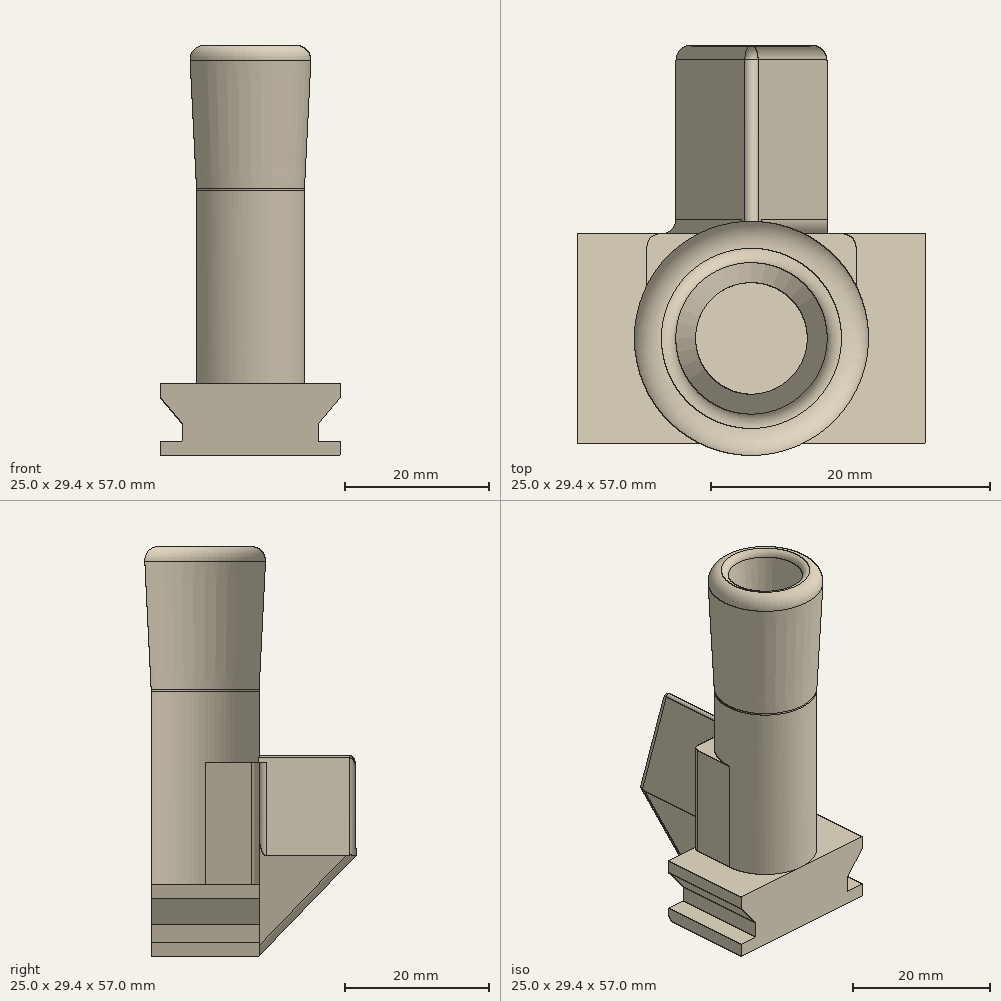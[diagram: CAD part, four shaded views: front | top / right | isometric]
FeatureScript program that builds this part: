
annotation { "Feature Type Name" : "Feature", "Feature Type Description" : "" }
export const myFeature = defineFeature(function(context is Context, id is Id, definition is map)
    precondition{}
    {
        {
            var Q0;
            Q0=qCreatedBy(makeId("Front.planeOp"),FACE);
            var sketch = newSketch(context, id + "F0", { "sketchPlane" : qUnion([Q0])});
            skLineSegment(sketch, "E0", {"start": v(0, 0) * mm, "end": v(0, 17.87) * mm, "construction": true});
            skLineSegment(sketch, "E1", {"start": v(0, 0) * mm, "end": v(-12.5, 0) * mm});
            skLineSegment(sketch, "E2", {"start": v(-12.5, 0) * mm, "end": v(-12.5, 2) * mm});
            skLineSegment(sketch, "E3", {"start": v(-12.5, 2) * mm, "end": v(-9.5, 2) * mm});
            skLineSegment(sketch, "E4", {"start": v(-9.5, 2) * mm, "end": v(-9.5, 4.42) * mm});
            skLineSegment(sketch, "E5", {"start": v(-12.5, 8) * mm, "end": v(-12.5, 10) * mm});
            skLineSegment(sketch, "E6", {"start": v(-12.5, 10) * mm, "end": v(0, 10) * mm});
            skLineSegment(sketch, "E7.MirrorCS", {"start": v(0, 0) * mm, "end": v(12.5, 0) * mm});
            skLineSegment(sketch, "E8.MirrorCS", {"start": v(12.5, 10) * mm, "end": v(0, 10) * mm});
            skLineSegment(sketch, "E9.MirrorCS", {"start": v(12.5, 8) * mm, "end": v(12.5, 10) * mm});
            skLineSegment(sketch, "E10.MirrorCS", {"start": v(12.5, 0) * mm, "end": v(12.5, 2) * mm});
            skLineSegment(sketch, "E11.MirrorCS", {"start": v(12.5, 2) * mm, "end": v(9.5, 2) * mm});
            skLineSegment(sketch, "E12", {"start": v(-12.5, 8) * mm, "end": v(-9.5, 4.42) * mm});
            skPoint(sketch, "E13.orphan", {"position": v(-9.5, 5.59) * mm});
            skLineSegment(sketch, "E14.MirrorCS", {"start": v(12.5, 8) * mm, "end": v(9.5, 4.42) * mm});
            skLineSegment(sketch, "E15.MirrorCS", {"start": v(9.5, 2) * mm, "end": v(9.5, 4.42) * mm});
            skSolve(sketch);
        }
        {
            var Q0;
            Q0 = qSketchRegion(id + "F0", true);
            extrude(context, id + "F1", {"entities" : qUnion([Q0]), "depth" : 15 * mm});
        }
        {
            var Q0;
            Q0=makeQuery(id+"F1.opExtrude","SWEPT_FACE",FACE,{"disambiguationData":[OSD([sQuery(id+"F0.wireOp",EDGE,"E6"),sQuery(id+"F0.wireOp",EDGE,"E8.MirrorCS")])]});
            var sketch = newSketch(context, id + "F2", { "sketchPlane" : qUnion([Q0])});
            skLineSegment(sketch, "E16", {"start": v(0, 0) * mm, "end": v(0, -15) * mm, "construction": true});
            skLineSegment(sketch, "E17", {"start": v(-7.5, -7.5) * mm, "end": v(-7.5, 0) * mm});
            skLineSegment(sketch, "E18", {"start": v(-7.5, 0) * mm, "end": v(7.5, 0) * mm});
            skLineSegment(sketch, "E19", {"start": v(7.5, 0) * mm, "end": v(7.5, -7.5) * mm});
            skLineSegment(sketch, "E20", {"start": v(-7.5, -7.5) * mm, "end": v(0, -7.5) * mm, "construction": true});
            skLineSegment(sketch, "E21", {"start": v(0, -7.5) * mm, "end": v(7.5, -7.5) * mm, "construction": true});
            skArc(sketch, "E22", {"start": v(-7.5, -7.5) * mm, "mid": v(0, -15) * mm, "end": v(7.5, -7.5) * mm});
            skSolve(sketch);
        }
        {
            var Q0;
            Q0 = qSketchRegion(id + "F2", true);
            extrude(context, id + "F3", {"entities" : qUnion([Q0]), "operationType" : NewBodyOperationType.ADD, "depth" : 5 * mm});
        }
        {
            var Q0;
            Q0=makeQuery(id+"F3.opExtrude","CAP_FACE",FACE,{"disambiguationData":[OSD([sQuery(id+"F2.wireOp",EDGE,"E17"),sQuery(id+"F2.wireOp",EDGE,"E18"),sQuery(id+"F2.wireOp",EDGE,"E19"),sQuery(id+"F2.wireOp",EDGE,"E22")])],"isStart":false});
            var sketch = newSketch(context, id + "F4", { "sketchPlane" : qUnion([Q0])});
            skArc(sketch, "E23.0", {"start": v(-7.5, -7.5) * mm, "mid": v(0, -15) * mm, "end": v(7.5, -7.5) * mm});
            skCircle(sketch, "E24", {"center": v(0, -7.5) * mm, "radius": 4 * mm});
            skLineSegment(sketch, "E25", {"start": v(-7.5, -7.5) * mm, "end": v(-7.5, 0) * mm});
            skLineSegment(sketch, "E26", {"start": v(-7.5, 0) * mm, "end": v(7.5, 0) * mm});
            skLineSegment(sketch, "E27", {"start": v(7.5, 0) * mm, "end": v(7.5, -7.5) * mm});
            skSolve(sketch);
        }
        {
            var Q0;
            Q0 = qSketchRegion(id + "F4", true);
            extrude(context, id + "F5", {"entities" : qUnion([Q0]), "operationType" : NewBodyOperationType.ADD, "depth" : 12 * mm});
        }
        {
            var Q0;
            Q0=makeQuery(id+"F5.opExtrude","CAP_FACE",FACE,{"disambiguationData":[OSD([sQuery(id+"F4.wireOp",EDGE,"E23.0"),sQuery(id+"F4.wireOp",EDGE,"E24"),sQuery(id+"F4.wireOp",EDGE,"E25"),sQuery(id+"F4.wireOp",EDGE,"E26"),sQuery(id+"F4.wireOp",EDGE,"E27")])],"isStart":false});
            var sketch = newSketch(context, id + "F6", { "sketchPlane" : qUnion([Q0])});
            skCircle(sketch, "E28.0", {"center": v(0, -7.5) * mm, "radius": 4 * mm});
            skCircle(sketch, "E29", {"center": v(0, -7.5) * mm, "radius": 7.5 * mm});
            skSolve(sketch);
        }
        {
            var Q0;
            Q0 = qSketchRegion(id + "F6", true);
            extrude(context, id + "F7", {"entities" : qUnion([Q0]), "operationType" : NewBodyOperationType.ADD, "depth" : 10 * mm});
        }
        {
            var Q0;
            Q0=makeQuery(id+"F5.boolean.opBoolean","MERGE",FACE,{"derivedFrom":[makeQuery(id+"F3.boolean.opBoolean","MERGE",FACE,{"derivedFrom":[makeQuery(id+"F1.opExtrude","CAP_FACE",FACE,{"disambiguationData":[OSD([sQuery(id+"F0.wireOp",EDGE,"E1"),sQuery(id+"F0.wireOp",EDGE,"E2"),sQuery(id+"F0.wireOp",EDGE,"E3"),sQuery(id+"F0.wireOp",EDGE,"E4"),sQuery(id+"F0.wireOp",EDGE,"E5"),sQuery(id+"F0.wireOp",EDGE,"E6"),sQuery(id+"F0.wireOp",EDGE,"E7.MirrorCS"),sQuery(id+"F0.wireOp",EDGE,"E8.MirrorCS"),sQuery(id+"F0.wireOp",EDGE,"E9.MirrorCS"),sQuery(id+"F0.wireOp",EDGE,"E10.MirrorCS"),sQuery(id+"F0.wireOp",EDGE,"E11.MirrorCS"),sQuery(id+"F0.wireOp",EDGE,"E12"),sQuery(id+"F0.wireOp",EDGE,"E14.MirrorCS"),sQuery(id+"F0.wireOp",EDGE,"E15.MirrorCS")])],"isStart":true}),makeQuery(id+"F3.opExtrude","SWEPT_FACE",FACE,{"disambiguationData":[OSD([sQuery(id+"F2.wireOp",EDGE,"E18")])]})]}),makeQuery(id+"F5.opExtrude","SWEPT_FACE",FACE,{"disambiguationData":[OSD([sQuery(id+"F4.wireOp",EDGE,"E26")])]})]});
            var sketch = newSketch(context, id + "F8", { "sketchPlane" : qUnion([Q0])});
            skPoint(sketch, "E30.0", {"position": v(0, 27) * mm});
            skLineSegment(sketch, "E31", {"start": v(0, 27) * mm, "end": v(0, 0) * mm, "construction": true});
            skLineSegment(sketch, "E32", {"start": v(0, 25.99) * mm, "end": v(-4, 15) * mm});
            skLineSegment(sketch, "E33", {"start": v(-4, 15) * mm, "end": v(0, 15) * mm});
            skPoint(sketch, "E33.endSnap0", {"position": v(0, 13.5) * mm});
            skPoint(sketch, "E34.0", {"position": v(-7.5, 10) * mm});
            skLineSegment(sketch, "E35.MirrorCS", {"start": v(4, 15) * mm, "end": v(0, 15) * mm});
            skLineSegment(sketch, "E36.MirrorCS", {"start": v(0, 25.99) * mm, "end": v(4, 15) * mm});
            skSolve(sketch);
        }
        {
            var Q0;
            Q0 = qSketchRegion(id + "F8", true);
            extrude(context, id + "F9", {"entities" : qUnion([Q0]), "operationType" : NewBodyOperationType.REMOVE, "oppositeDirection" : true, "depth" : 8 * mm});
        }
        {
            var Q0;
            Q0=qCreatedBy(makeId("Front.planeOp"),FACE);
            cPlane(context, id + "F10", {"entities" : qUnion([Q0]), "cplaneType" : CPlaneType.OFFSET, "offset" : 7.5 * mm, "width" : 150 * mm, "height" : 150 * mm});
        }
        {
            var Q0;
            Q0=qCreatedBy(id+"F10.planeOp",FACE);
            var sketch = newSketch(context, id + "F11", { "sketchPlane" : qUnion([Q0])});
            skLineSegment(sketch, "E37.0", {"start": v(-4, 37) * mm, "end": v(4, 37) * mm, "construction": true});
            skLineSegment(sketch, "E38.0", {"start": v(-7.5, 37) * mm, "end": v(7.5, 37) * mm, "construction": true});
            skLineSegment(sketch, "E39", {"start": v(4, 37) * mm, "end": v(7.5, 37) * mm});
            skLineSegment(sketch, "E40", {"start": v(7.5, 37) * mm, "end": v(8.5, 57) * mm});
            skLineSegment(sketch, "E41", {"start": v(8.5, 57) * mm, "end": v(5.5, 57) * mm});
            skLineSegment(sketch, "E42", {"start": v(5.5, 57) * mm, "end": v(4, 37) * mm});
            skPoint(sketch, "E43", {"position": v(0, 37) * mm});
            skLineSegment(sketch, "E44", {"start": v(0, 37) * mm, "end": v(0, 68.07) * mm, "construction": true});
            skSolve(sketch);
        }
        {
            var Q0;
            Q0 = qSketchRegion(id + "F11", true);
            var Q1;
            Q1=makeQuery(id+"F7.opExtrude","CAP_EDGE",EDGE,{"disambiguationData":[OSD([sQuery(id+"F6.wireOp",EDGE,"E29")])],"isStart":false});
            revolve(context, id + "F12", {"operationType" : NewBodyOperationType.ADD, "entities" : qUnion([Q0]), "axis" : qUnion([Q1]), "revolveType" : RevolveType.FULL});
        }
        {
            var Q0;
            Q0=makeQuery(id+"F12.opRevolve","SWEPT_EDGE",EDGE,{"disambiguationData":[OSD([sQuery(id+"F11.wireOp",EDGE,"E40"),sQuery(id+"F11.wireOp",EDGE,"E41")])]});
            fillet(context, id + "F13", {"entities" : qUnion([Q0]), "radius" : 2 * mm, "tangentPropagation" : true, "allowEdgeOverflow" : false});
        }
        {
            var Q0;
            Q0=makeQuery(id+"F12.boolean.opBoolean","MERGE",EDGE,{"derivedFrom":[makeQuery(id+"F7.opExtrude","CAP_EDGE",EDGE,{"disambiguationData":[OSD([sQuery(id+"F6.wireOp",EDGE,"E29")])],"isStart":false}),makeQuery(id+"F12.opRevolve","SWEPT_EDGE",EDGE,{"disambiguationData":[OSD([sQuery(id+"F11.wireOp",EDGE,"E39"),sQuery(id+"F11.wireOp",EDGE,"E40")])]})]});
            fillet(context, id + "F14", {"entities" : qUnion([Q0]), "radius" : 5 * mm, "tangentPropagation" : true, "allowEdgeOverflow" : false});
        }
        {
            var Q0;
            Q0=makeQuery(id+"F12.opRevolve","SWEPT_EDGE",EDGE,{"disambiguationData":[OSD([sQuery(id+"F11.wireOp",EDGE,"E41"),sQuery(id+"F11.wireOp",EDGE,"E42")])]});
            fillet(context, id + "F15", {"entities" : qUnion([Q0]), "radius" : 1 * mm, "tangentPropagation" : true, "allowEdgeOverflow" : false});
        }
        {
            var Q0;
            Q0=qCreatedBy(makeId("Front.planeOp"),FACE);
            cPlane(context, id + "F16", {"entities" : qUnion([Q0]), "cplaneType" : CPlaneType.OFFSET, "offset" : 1.5 * mm, "width" : 150 * mm, "height" : 150 * mm});
        }
        {
            var Q0;
            Q0=qCreatedBy(id+"F16.planeOp",FACE);
            var sketch = newSketch(context, id + "F17", { "sketchPlane" : qUnion([Q0])});
            skLineSegment(sketch, "E45", {"start": v(0, 28.91) * mm, "end": v(-5.43, 14) * mm});
            skLineSegment(sketch, "E46", {"start": v(-5.43, 14) * mm, "end": v(0, 14) * mm});
            skLineSegment(sketch, "E47", {"start": v(0, 14) * mm, "end": v(0, 28.91) * mm, "construction": true});
            skLineSegment(sketch, "E48.MirrorCS", {"start": v(0, 28.91) * mm, "end": v(5.43, 14) * mm});
            skLineSegment(sketch, "E49.MirrorCS", {"start": v(5.43, 14) * mm, "end": v(0, 14) * mm});
            skLineSegment(sketch, "E50.0", {"start": v(0, 25.99) * mm, "end": v(4, 15) * mm});
            skLineSegment(sketch, "E51.0", {"start": v(4, 15) * mm, "end": v(-4, 15) * mm});
            skLineSegment(sketch, "E52.0", {"start": v(0, 25.99) * mm, "end": v(-4, 15) * mm});
            skSolve(sketch);
        }
        {
            var Q0;
            Q0 = qSketchRegion(id + "F17", true);
            extrude(context, id + "F18", {"entities" : qUnion([Q0]), "operationType" : NewBodyOperationType.ADD, "oppositeDirection" : true, "depth" : 15 * mm});
        }
        {
            var Q0;
            Q0=makeQuery(id+"F18.opExtrude","SWEPT_EDGE",EDGE,{"disambiguationData":[OSD([sQuery(id+"F17.wireOp",EDGE,"E45"),sQuery(id+"F17.wireOp",EDGE,"E48.MirrorCS")])]});
            fillet(context, id + "F19", {"entities" : qUnion([Q0]), "radius" : .5 * mm, "tangentPropagation" : true, "allowEdgeOverflow" : false});
        }
        {
            var Q0;
            Q0=qCreatedBy(makeId("Right.planeOp"),FACE);
            var sketch = newSketch(context, id + "F20", { "sketchPlane" : qUnion([Q0])});
            skPoint(sketch, "E53.0", {"position": v(0, 14) * mm});
            skPoint(sketch, "E54.0", {"position": v(13.5, 14) * mm});
            skLineSegment(sketch, "E55", {"start": v(13.5, 14) * mm, "end": v(0, 14) * mm});
            skLineSegment(sketch, "E56", {"start": v(0, 0) * mm, "end": v(0, 14) * mm});
            skLineSegment(sketch, "E57", {"start": v(0, 0) * mm, "end": v(13.5, 14) * mm});
            skSolve(sketch);
        }
        {
            var Q0;
            Q0 = qSketchRegion(id + "F20", true);
            var Q1;
            Q1=makeQuery(id+"F18.opExtrude","CAP_VERTEX",VERTEX,{"disambiguationData":[OSD([sQuery(id+"F17.wireOp",EDGE,"E48.MirrorCS"),sQuery(id+"F17.wireOp",EDGE,"E49.MirrorCS")])],"isStart":false});
            var Q2;
            Q2=makeQuery(id+"F18.opExtrude","CAP_VERTEX",VERTEX,{"disambiguationData":[OSD([sQuery(id+"F17.wireOp",EDGE,"E45"),sQuery(id+"F17.wireOp",EDGE,"E46")])],"isStart":false});
            extrude(context, id + "F21", {"entities" : qUnion([Q0]), "operationType" : NewBodyOperationType.ADD, "endBound" : BoundingType.UP_TO_VERTEX, "endBoundEntityVertex" : qUnion([Q1]), "depth" : 5 * mm, "hasSecondDirection" : true, "secondDirectionBound" : SecondDirectionBoundingType.UP_TO_VERTEX, "secondDirectionOppositeDirection" : true, "secondDirectionBoundEntityVertex" : qUnion([Q2]), "secondDirectionDepth" : 25 * mm});
        }
        {
            var Q0;
            Q0=makeQuery(id+"F21.opExtrude","CAP_EDGE",EDGE,{"disambiguationData":[OSD([sQuery(id+"F20.wireOp",EDGE,"E56")])],"isStart":true});
            var Q1;
            Q1=makeQuery(id+"F21.opExtrude","CAP_EDGE",EDGE,{"disambiguationData":[OSD([sQuery(id+"F20.wireOp",EDGE,"E56")])],"isStart":false});
            var Q2;
            Q2=makeQuery(id+"F18.boolean.opBoolean","INTERSECT",EDGE,{"derivedFrom":[makeQuery(id+"F5.boolean.opBoolean","MERGE",FACE,{"derivedFrom":[makeQuery(id+"F3.boolean.opBoolean","MERGE",FACE,{"derivedFrom":[makeQuery(id+"F1.opExtrude","CAP_FACE",FACE,{"disambiguationData":[OSD([sQuery(id+"F0.wireOp",EDGE,"E1"),sQuery(id+"F0.wireOp",EDGE,"E2"),sQuery(id+"F0.wireOp",EDGE,"E3"),sQuery(id+"F0.wireOp",EDGE,"E4"),sQuery(id+"F0.wireOp",EDGE,"E5"),sQuery(id+"F0.wireOp",EDGE,"E6"),sQuery(id+"F0.wireOp",EDGE,"E7.MirrorCS"),sQuery(id+"F0.wireOp",EDGE,"E8.MirrorCS"),sQuery(id+"F0.wireOp",EDGE,"E9.MirrorCS"),sQuery(id+"F0.wireOp",EDGE,"E10.MirrorCS"),sQuery(id+"F0.wireOp",EDGE,"E11.MirrorCS"),sQuery(id+"F0.wireOp",EDGE,"E12"),sQuery(id+"F0.wireOp",EDGE,"E14.MirrorCS"),sQuery(id+"F0.wireOp",EDGE,"E15.MirrorCS")])],"isStart":true}),makeQuery(id+"F3.opExtrude","SWEPT_FACE",FACE,{"disambiguationData":[OSD([sQuery(id+"F2.wireOp",EDGE,"E18")])]})]}),makeQuery(id+"F5.opExtrude","SWEPT_FACE",FACE,{"disambiguationData":[OSD([sQuery(id+"F4.wireOp",EDGE,"E26")])]})]}),makeQuery(id+"F18.opExtrude","SWEPT_FACE",FACE,{"disambiguationData":[OSD([sQuery(id+"F17.wireOp",EDGE,"E48.MirrorCS")])]})]});
            var Q3;
            Q3=makeQuery(id+"F18.boolean.opBoolean","INTERSECT",EDGE,{"derivedFrom":[makeQuery(id+"F5.boolean.opBoolean","MERGE",FACE,{"derivedFrom":[makeQuery(id+"F3.boolean.opBoolean","MERGE",FACE,{"derivedFrom":[makeQuery(id+"F1.opExtrude","CAP_FACE",FACE,{"disambiguationData":[OSD([sQuery(id+"F0.wireOp",EDGE,"E1"),sQuery(id+"F0.wireOp",EDGE,"E2"),sQuery(id+"F0.wireOp",EDGE,"E3"),sQuery(id+"F0.wireOp",EDGE,"E4"),sQuery(id+"F0.wireOp",EDGE,"E5"),sQuery(id+"F0.wireOp",EDGE,"E6"),sQuery(id+"F0.wireOp",EDGE,"E7.MirrorCS"),sQuery(id+"F0.wireOp",EDGE,"E8.MirrorCS"),sQuery(id+"F0.wireOp",EDGE,"E9.MirrorCS"),sQuery(id+"F0.wireOp",EDGE,"E10.MirrorCS"),sQuery(id+"F0.wireOp",EDGE,"E11.MirrorCS"),sQuery(id+"F0.wireOp",EDGE,"E12"),sQuery(id+"F0.wireOp",EDGE,"E14.MirrorCS"),sQuery(id+"F0.wireOp",EDGE,"E15.MirrorCS")])],"isStart":true}),makeQuery(id+"F3.opExtrude","SWEPT_FACE",FACE,{"disambiguationData":[OSD([sQuery(id+"F2.wireOp",EDGE,"E18")])]})]}),makeQuery(id+"F5.opExtrude","SWEPT_FACE",FACE,{"disambiguationData":[OSD([sQuery(id+"F4.wireOp",EDGE,"E26")])]})]}),makeQuery(id+"F18.opExtrude","SWEPT_FACE",FACE,{"disambiguationData":[OSD([sQuery(id+"F17.wireOp",EDGE,"E45")])]})]});
            fillet(context, id + "F22", {"entities" : qUnion([Q0, Q1, Q2, Q3]), "radius" : 1 * mm, "tangentPropagation" : true, "allowEdgeOverflow" : false});
        }
        {
            var Q0;
            Q0=makeQuery(id+"F21.opExtrude","CAP_EDGE",EDGE,{"disambiguationData":[OSD([sQuery(id+"F20.wireOp",EDGE,"E57")])],"isStart":true});
            var Q1;
            Q1=makeQuery(id+"F18.opExtrude","CAP_EDGE",EDGE,{"disambiguationData":[OSD([sQuery(id+"F17.wireOp",EDGE,"E45")])],"isStart":false});
            var Q2;
            Q2=makeQuery(id+"F21.opExtrude","CAP_EDGE",EDGE,{"disambiguationData":[OSD([sQuery(id+"F20.wireOp",EDGE,"E57")])],"isStart":false});
            fillet(context, id + "F23", {"entities" : qUnion([Q0, Q1, Q2]), "radius" : 1 * mm, "tangentPropagation" : true, "allowEdgeOverflow" : false});
        }
        {
            var Q0;
            Q0=makeQuery(id+"F5.boolean.opBoolean","MERGE",EDGE,{"derivedFrom":[makeQuery(id+"F3.opExtrude","SWEPT_EDGE",EDGE,{"disambiguationData":[OSD([sQuery(id+"F0.wireOp",EDGE,"E6"),sQuery(id+"F0.wireOp",EDGE,"E8.MirrorCS"),sQuery(id+"F2.wireOp",EDGE,"E18"),sQuery(id+"F2.wireOp",EDGE,"E19")])]}),makeQuery(id+"F5.opExtrude","SWEPT_EDGE",EDGE,{"disambiguationData":[OSD([sQuery(id+"F4.wireOp",EDGE,"E26"),sQuery(id+"F4.wireOp",EDGE,"E27")])]})]});
            var Q1;
            Q1=makeQuery(id+"F5.boolean.opBoolean","MERGE",EDGE,{"derivedFrom":[makeQuery(id+"F3.opExtrude","SWEPT_EDGE",EDGE,{"disambiguationData":[OSD([sQuery(id+"F0.wireOp",EDGE,"E6"),sQuery(id+"F0.wireOp",EDGE,"E8.MirrorCS"),sQuery(id+"F2.wireOp",EDGE,"E17"),sQuery(id+"F2.wireOp",EDGE,"E18")])]}),makeQuery(id+"F5.opExtrude","SWEPT_EDGE",EDGE,{"disambiguationData":[OSD([sQuery(id+"F4.wireOp",EDGE,"E25"),sQuery(id+"F4.wireOp",EDGE,"E26")])]})]});
            fillet(context, id + "F24", {"entities" : qUnion([Q0, Q1]), "radius" : 1 * mm, "tangentPropagation" : true, "allowEdgeOverflow" : false});
        }
        {
            var Q0;
            {var subQ0=sQuery(id+"F2.wireOp",EDGE,"E18");var subQ1=makeQuery(id+"F9.opExtrude","SWEPT_FACE",FACE,{"disambiguationData":[OSD([sQuery(id+"F8.wireOp",EDGE,"E36.MirrorCS")])]});Q0=makeQuery(id+"F23.opFillet","BLEND_EDGE",EDGE,{"blendedFrom":[makeQuery(id+"F18.opExtrude","CAP_EDGE",EDGE,{"disambiguationData":[OSD([sQuery(id+"F17.wireOp",EDGE,"E45")])],"isStart":false}),makeQuery(id+"F18.boolean.opBoolean","MERGE",FACE,{"derivedFrom":[makeQuery(id+"F9.boolean.opBoolean","COPY",FACE,{"disambiguationData":[TD([makeQuery(id+"F3.opExtrude","SWEPT_FACE",FACE,{"disambiguationData":[OSD([subQ0])]})])],"derivedFrom":subQ1}),makeQuery(id+"F18.opExtrude","SWEPT_FACE",FACE,{"disambiguationData":[OSD([sQuery(id+"F17.wireOp",EDGE,"E52.0")])]})]})],"blendedInto":[makeQuery(id+"F18.boolean.opBoolean","MERGE",FACE,{"derivedFrom":[makeQuery(id+"F9.boolean.opBoolean","COPY",FACE,{"disambiguationData":[TD([makeQuery(id+"F3.opExtrude","SWEPT_FACE",FACE,{"disambiguationData":[OSD([subQ0])]})])],"derivedFrom":subQ1}),makeQuery(id+"F18.opExtrude","SWEPT_FACE",FACE,{"disambiguationData":[OSD([sQuery(id+"F17.wireOp",EDGE,"E52.0")])]})]})]});}
            var Q1;
            {var subQ0=sQuery(id+"F2.wireOp",EDGE,"E18");var subQ1=makeQuery(id+"F9.opExtrude","SWEPT_FACE",FACE,{"disambiguationData":[OSD([sQuery(id+"F8.wireOp",EDGE,"E32")])]});Q1=makeQuery(id+"F23.opFillet","BLEND_EDGE",EDGE,{"blendedFrom":[makeQuery(id+"F18.opExtrude","CAP_EDGE",EDGE,{"disambiguationData":[OSD([sQuery(id+"F17.wireOp",EDGE,"E48.MirrorCS")])],"isStart":false}),makeQuery(id+"F18.boolean.opBoolean","MERGE",FACE,{"derivedFrom":[makeQuery(id+"F9.boolean.opBoolean","COPY",FACE,{"disambiguationData":[TD([makeQuery(id+"F3.opExtrude","SWEPT_FACE",FACE,{"disambiguationData":[OSD([subQ0])]})])],"derivedFrom":subQ1}),makeQuery(id+"F18.opExtrude","SWEPT_FACE",FACE,{"disambiguationData":[OSD([sQuery(id+"F17.wireOp",EDGE,"E50.0")])]})]})],"blendedInto":[makeQuery(id+"F18.boolean.opBoolean","MERGE",FACE,{"derivedFrom":[makeQuery(id+"F9.boolean.opBoolean","COPY",FACE,{"disambiguationData":[TD([makeQuery(id+"F3.opExtrude","SWEPT_FACE",FACE,{"disambiguationData":[OSD([subQ0])]})])],"derivedFrom":subQ1}),makeQuery(id+"F18.opExtrude","SWEPT_FACE",FACE,{"disambiguationData":[OSD([sQuery(id+"F17.wireOp",EDGE,"E50.0")])]})]})]});}
            fillet(context, id + "F25", {"entities" : qUnion([Q0, Q1]), "radius" : .25 * mm, "tangentPropagation" : true, "allowEdgeOverflow" : false});
        }
    });
